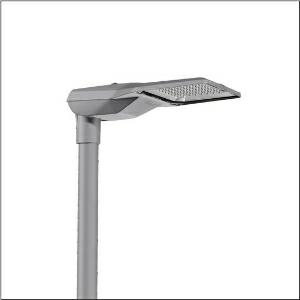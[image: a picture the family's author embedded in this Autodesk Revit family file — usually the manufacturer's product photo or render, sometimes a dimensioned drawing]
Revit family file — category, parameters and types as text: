
# Revit family: streetlight_sl_21_midi___st0_8a_5xe3c33s08lb_6676
name_source: partatom
category: Lighting Fixtures
units: mm (PartAtom-declared; Revit-internal decimal feet)

## family parameters
Cut with Voids When Loaded = No
Host = Face
Light Source = No
Part Type = Normal
Room Calculation Point = No
Round Connector Dimension = Use Diameter
Shared = No

## types (1)
- --- (1 x LED, 14340 lm, 99.6 W, 3000K)
    Apparent Load = 100 VA
    CIE Flux Codes = 38 75 97 100 100
    Color Rendering = 70
    Color Temperature = 3000K
    Default Elevation = 1800 mm
    Description = Streetlight SL 21 midi, mast luminaire, primary light control with lens, of PMMA, primary optical cover: cover, of toughened safety glass, transparent, light distribution: ST0.8a, light emission: direct distribution, primary light characteristic: asymmetric, installation type: side-entry, post-top, LED, High Power LED, rated luminous flux: 14.340lm, luminous efficacy: 144lm/W, light colour: 730, colour temperature: 3000K, control gear: D4i, control: overheat protection, constant luminous flux control, time-dependent luminous flux control, flexible luminous flux parameterisation, pre-setting: logarithmic dimming characteristic, mains connection: 230..240V, AC, 50/60Hz, start of lifetime: 100W, end of service life: 102W, reduction: 46W, luminaire housing, of diecast aluminium, powder-coated, Siteco® metallic grey (DB 702S), corrosivity category C5 mid according to DIN EN ISO 12944, please order mast flange separately, inclination adjustable: 0°, 5°, 10°, 15°, sealing non-destructively replaceable, multi-level sealing system, length: 644mm, width: 335mm, height: 110mm, mast flange for spigot size: 42mm (side-entry): 5XC10008XM4, 60/48mm (side-entry/post-top): 5XC10108XM2, 76/60mm (side-entry/post-top): 5XC10108XM1, mounting height: 4..8m, Smart Interface above, protection rating (complete): IP66, insulation class (complete): insulation class II (safety insulation), certification: CE, ENEC, ENEC+, VDE, impact resistance: IK10, permissible operating ambient temperature for outdoor applications: -40..+50°C, standard-compliant lighting for roads and squares, packaging unit: 1 piece

Light Distribution: ST0.8a
    Height = 111 mm
    Lamp = 1 x LED
    Lamp Light Flux = 14340 lm
    Lamp Power = 99.6 W
    Lamp count = 1
    Length = 644 mm
    Luminous efficacy = 144 lm/W
    Manufacturer = Siteco
    ModVariant = No
    Model = 5XE3C33S08LB
    Number of Poles = 1
    OnlyDefault = Yes
    Power Factor = 1
    Product Name = Streetlight SL 21 midi | ST0.8a
    Product group = mast luminaire | pylon top
    ProductGroupID = 6100
    Protection Class = Protection class II
    Protection Degree = IP 66
    RLX_Detail_Level = 1
    RLX_Emergency_Light_Flux = 0 lm
    RLX_Emergency_Type = 0
    RLX_Emergency_Type_DB = No
    RlxData = <blob elided: 26881 chars, md5=86482938>
    Socket = socket
    Standby Power = 0 W
    System Light Flux = 14340 lm
    System Power = 100 W
    Type Comments = factory setting: luminous flux: 100 % | dim-lin: 254 | 1020 mA
    Type Image = l_1004302.jpg
    URL = http://relux.com
    VarID = @adj_011301
    Voltage = 0 V
    Weight = 0.00 kg
    Width = 336 mm

## geometry (parser evidence)
native form markers: Blend x4, Sweep x11
no freeform markers — native parametric forms only
